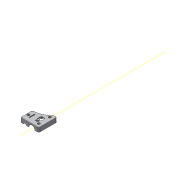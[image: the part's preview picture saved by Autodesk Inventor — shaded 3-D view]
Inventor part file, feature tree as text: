
AUTODESK INVENTOR PART (.ipt)
format: ipt  version: 2016 (Build 200138000, 138)  size: 925,184 bytes
history: native  units: in
note: dims shown in document units (in); Inventor stores cm internally (conversion verified against a paired STEP export)
features: sketch x21, extrude x17, projected_geometry x11, fillet x6, plane x3, other x2, loft x1, imported_body x1
ambient origin geometry x8: Origin, YZ Plane, XZ Plane, XY Plane, X Axis, Y Axis, Z Axis, Center Point
bodies: Solid1 (feature_tree)
feature tree (62):
  other  "032-Fe_Top_Cover-0601-3_stp.ipt1"
  sketch  "Sketch2"  dims[d7=0.1181in d8=0.1181in]
  other  "Work Axis1"
  plane  "Work Plane1"
  extrude  "Extrusion2"  Depth=0.1181in
  plane  "Work Plane3"
  loft  "Loft1"
  extrude  "Extrusion4"  Depth=0.1575in
  extrude  "Extrusion5"  TaperAngle=0.0deg  [1 undecoded]
  extrude  "Extrusion6"  TaperAngle=0.0deg  [1 undecoded]
  extrude  "Extrusion7"  Depth=0.1181in
  extrude  "Extrusion8"  Depth=0.0591in
  fillet  "Fillet5"  Radius=0.0197in
  fillet  "Fillet6"  Radius=0.0787in
  extrude  "Extrusion9"  Depth=0.3937in
  extrude  "Extrusion10"  Depth=0.7087in
  extrude  "Extrusion12"  Depth=0.0118in
  extrude  "Extrusion13"  Depth=0.0315in
  extrude  "Extrusion14"  Depth=0.2559in
  extrude  "Extrusion15"  Depth=0.3937in TaperAngle=0.0deg
  sketch  "Sketch20"  dims[d78=0.1575in d79=0.1575in]
  extrude  "Extrusion17"  Depth=0.5512in
  extrude  "Extrusion19"  Depth=0.2362in
  extrude  "Extrusion20"  Depth=0.4252in
  fillet  "Fillet7"  Radius=0.4724in
  fillet  "Fillet8"  Radius=0.4724in
  extrude  "Extrusion21"  Depth=0.1575in
  extrude  "Extrusion22"  Depth=0.4724in
  fillet  "Fillet9"  Radius=0.0394in
  fillet  "Fillet10"  Radius=0.0039in
  imported_body  "Base1"
  sketch  "Sketch3"  dims[d9=0.3937in d10=0.0137in d14=0.1575in d15=0.2047in]
  plane  "Work Plane2"
  sketch  "Sketch5"  dims[d16=0.0906in d17=0.1575in]
  sketch  "Sketch6"  dims[d18=0.4331in d19=0.0in d20=90.0deg]
  sketch  "Sketch7"  dims[d21=0.0in d22=90.0deg d23=0.0in d24=90.0deg]
  sketch  "Sketch8"  dims[d25=0.3937in d26=0.0in d29=0.1181in]
  sketch  "Sketch9"  dims[d30=0.0591in d31=0.0591in d32=0.0197in d33=0.0in d34=0.0787in]
  sketch  "Sketch10"  dims[d35=0.1575in d36=0.3937in d37=0.0137in]
  sketch  "Sketch11"  dims[d39=0.0in d40=0.0in d42=0.7087in]
  sketch  "Sketch12"  dims[d43=0.3543in d44=-0.0137in d45=0.0118in]
  sketch  "Sketch13"  dims[d46=0.0118in d47=0.0315in d48=-0.0103in]
  projected_geometry  "Projected Loop4"
  sketch  "Sketch14"  dims[d49=0.0236in d50=0.0in d51=0.2559in]
  sketch  "Sketch16"  dims[d55=0.4724in d56=0.3937in d57=0.0in]
  projected_geometry  "Projected Loop6"
  sketch  "Sketch17"  dims[d58=0.4724in d59=0.0137in d60=0.5512in]
  projected_geometry  "Projected Loop7"
  sketch  "Sketch18"  dims[d61=0.5394in d62=0.2362in]
  projected_geometry  "Projected Loop8"
  sketch  "Sketch19"  dims[d63=0.4724in d64=0.0in d65=0.4252in d66=0.4724in d67=0.0137in d74=0.4724in d75=0.0137in]
  projected_geometry  "Projected Loop9"
  projected_geometry  "Projected Loop10"
  projected_geometry  "Projected Loop11"
  sketch  "Sketch21"  dims[d80=0.4724in d81=-0.0137in d82=0.4724in d83=0.0137in d84=0.0394in d85=0.0039in]
  projected_geometry  "Projected Loop12"
  sketch  "Sketch22"  dims[d86=0.4724in d87=0.0103in]
  projected_geometry  "Projected Loop13"
  sketch  "Sketch23"  dims[d88=0.4724in d89=0.0103in]
  projected_geometry  "Projected Loop14"
  sketch  "Sketch24"  dims[d90=0.0118in d91=0.0394in]
  projected_geometry  "Projected Loop15"
note: 2 required parameter values undecoded (feature->parameter linkage not recoverable at this tier; creation-order binding heuristic only, values carry confidence <= 0.55)
